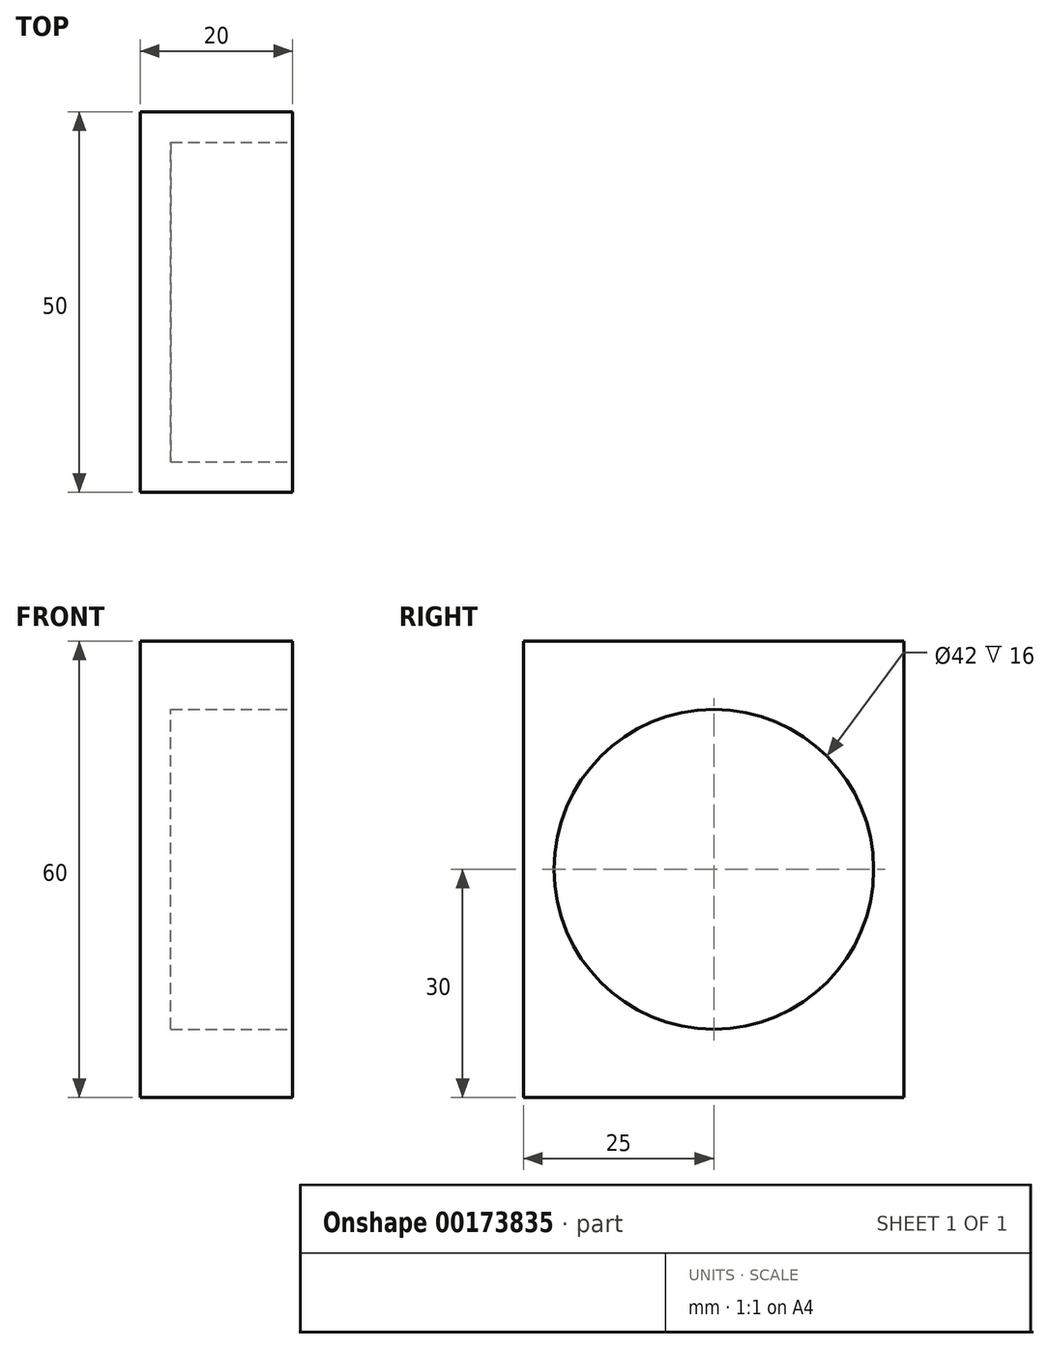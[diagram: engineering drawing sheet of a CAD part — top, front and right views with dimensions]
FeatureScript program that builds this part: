
annotation { "Feature Type Name" : "Feature", "Feature Type Description" : "" }
export const myFeature = defineFeature(function(context is Context, id is Id, definition is map)
    precondition{}
    {
        {
            var Q0;
            Q0=qCreatedBy(makeId("Front.planeOp"),FACE);
            var sketch = newSketch(context, id + "F0", { "sketchPlane" : qUnion([Q0])});
            skLineSegment(sketch, "E0.bottom", {"start": v(0, 0) * mm, "end": v(20, 0) * mm});
            skLineSegment(sketch, "E0.top", {"start": v(0, 60) * mm, "end": v(20, 60) * mm});
            skLineSegment(sketch, "E0.left", {"start": v(0, 0) * mm, "end": v(0, 60) * mm});
            skLineSegment(sketch, "E0.right", {"start": v(20, 0) * mm, "end": v(20, 60) * mm});
            skSolve(sketch);
        }
        {
            var Q0;
            Q0 = qSketchRegion(id + "F0", true);
            extrude(context, id + "F1", {"entities" : qUnion([Q0]), "depth" : 50 * mm});
        }
        {
            var Q0;
            Q0=makeQuery(id+"F1.opExtrude","SWEPT_FACE",FACE,{"disambiguationData":[OSD([sQuery(id+"F0.wireOp",EDGE,"E0.right")])]});
            var sketch = newSketch(context, id + "F2", { "sketchPlane" : qUnion([Q0])});
            skCircle(sketch, "E1", {"center": v(-25, 30) * mm, "radius": 21 * mm});
            skSolve(sketch);
        }
        {
            var Q0;
            Q0 = qSketchRegion(id + "F2", true);
            extrude(context, id + "F3", {"entities" : qUnion([Q0]), "operationType" : NewBodyOperationType.REMOVE, "oppositeDirection" : true, "depth" : 16 * mm});
        }
    });
